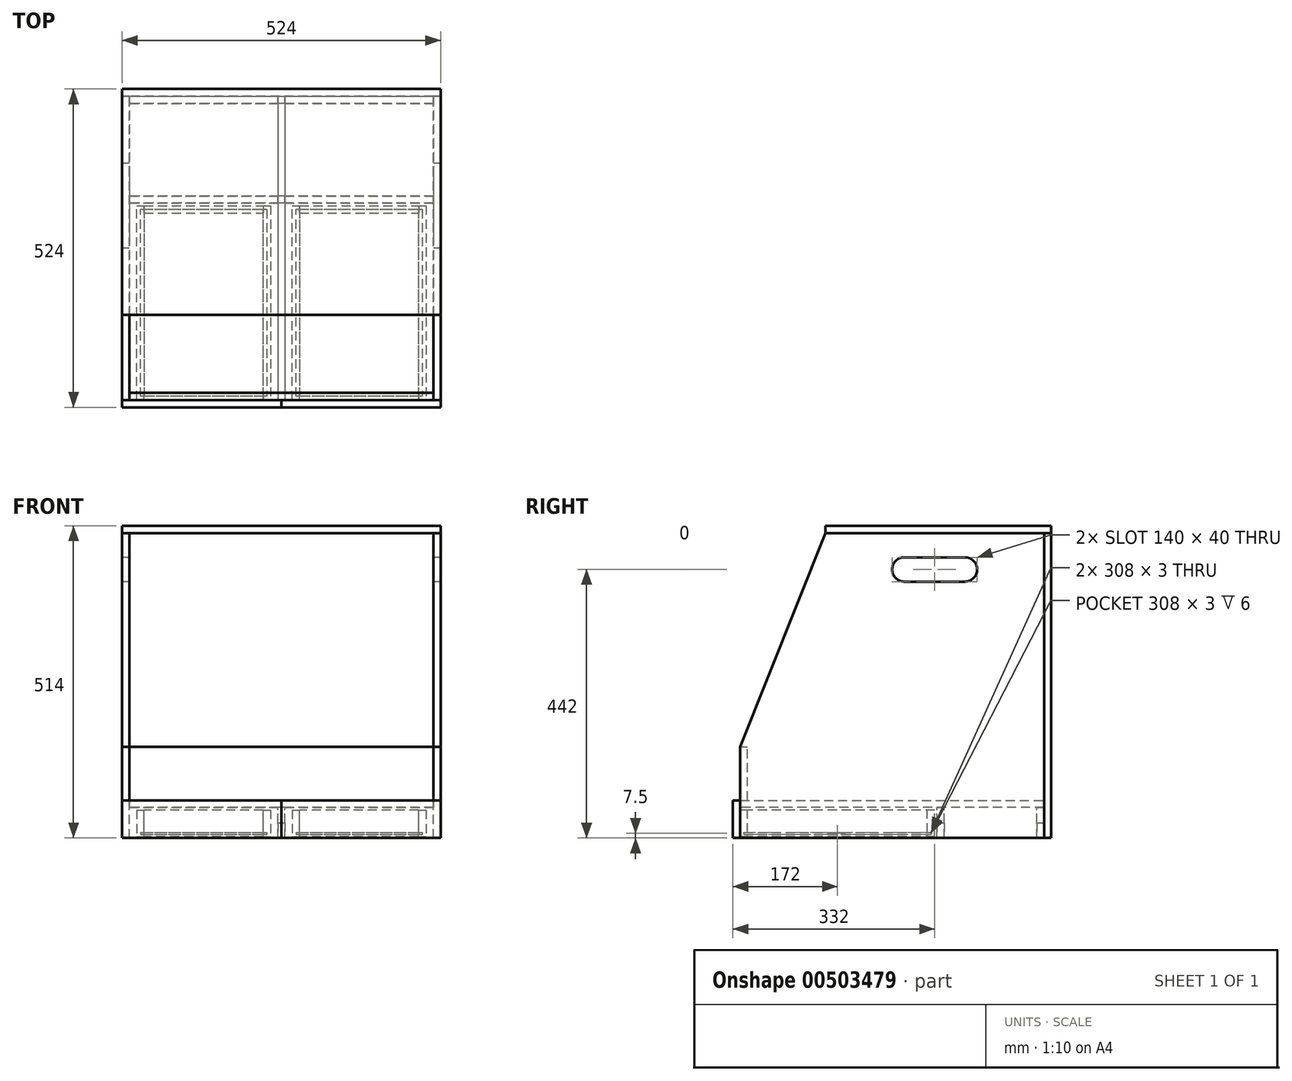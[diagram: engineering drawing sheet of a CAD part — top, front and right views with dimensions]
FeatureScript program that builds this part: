
annotation { "Feature Type Name" : "Feature", "Feature Type Description" : "" }
export const myFeature = defineFeature(function(context is Context, id is Id, definition is map)
    precondition{}
    {
        {
            var Q0;
            Q0=qCreatedBy(makeId("Top.planeOp"),FACE);
            var sketch = newSketch(context, id + "F0", { "sketchPlane" : qUnion([Q0])});
            skLineSegment(sketch, "E0.bottom", {"start": v(250, -250) * mm, "end": v(-250, -250) * mm});
            skLineSegment(sketch, "E0.top", {"start": v(250, 250) * mm, "end": v(-250, 250) * mm});
            skLineSegment(sketch, "E0.left", {"start": v(250, -250) * mm, "end": v(250, 250) * mm});
            skLineSegment(sketch, "E0.right", {"start": v(-250, -250) * mm, "end": v(-250, 250) * mm});
            skPoint(sketch, "E0.middle", {"position": v(0, 0) * mm});
            skSolve(sketch);
        }
        {
            var Q0;
            Q0 = qSketchRegion(id + "F0", true);
            extrude(context, id + "F1", {"entities" : qUnion([Q0]), "depth" : 12 * mm, "offsetDistance" : 25 * mm});
        }
        {
            var Q0;
            Q0=qCreatedBy(makeId("Right.planeOp"),FACE);
            var sketch = newSketch(context, id + "F2", { "sketchPlane" : qUnion([Q0])});
            skLineSegment(sketch, "E1.bottom", {"start": v(250, -25) * mm, "end": v(-250, -25) * mm});
            skLineSegment(sketch, "E1.top", {"start": v(250, 25) * mm, "end": v(-250, 25) * mm});
            skLineSegment(sketch, "E1.left", {"start": v(250, -25) * mm, "end": v(250, 25) * mm});
            skLineSegment(sketch, "E1.right", {"start": v(-250, -25) * mm, "end": v(-250, 25) * mm});
            skPoint(sketch, "E1.middle", {"position": v(0, 0) * mm});
            skSolve(sketch);
        }
        {
            var Q0;
            Q0 = qSketchRegion(id + "F2", true);
            extrude(context, id + "F3", {"entities" : qUnion([Q0]), "endBound" : BoundingType.SYMMETRIC, "depth" : 12 * mm, "offsetDistance" : 25 * mm});
        }
        {
            var Q0;
            Q0=makeQuery(id+"F3.opExtrude","SWEPT_BODY",BODY,{"disambiguationData":[OSD([sQuery(id+"F2.wireOp",EDGE,"E1.bottom"),sQuery(id+"F2.wireOp",EDGE,"E1.top"),sQuery(id+"F2.wireOp",EDGE,"E1.left"),sQuery(id+"F2.wireOp",EDGE,"E1.right")])]});
            transform(context, id + "F4", {"entities" : qUnion([Q0]), "transformType" : TransformType.TRANSLATION_3D, "dx" : 0 * mm, "dy" : 0 * mm, "dz" : -25 * mm, "makeCopy" : false});
        }
        {
            var Q0;
            Q0=qCreatedBy(makeId("Front.planeOp"),FACE);
            var sketch = newSketch(context, id + "F5", { "sketchPlane" : qUnion([Q0])});
            skLineSegment(sketch, "E2.bottom", {"start": v(250, -25) * mm, "end": v(-250, -25) * mm});
            skLineSegment(sketch, "E2.left", {"start": v(250, -25) * mm, "end": v(250, 25) * mm});
            skLineSegment(sketch, "E2.right", {"start": v(-250, -25) * mm, "end": v(-250, 25) * mm});
            skPoint(sketch, "E2.middle", {"position": v(0, 0) * mm});
            skLineSegment(sketch, "E3", {"start": v(-250, 25) * mm, "end": v(-6, 25) * mm});
            skLineSegment(sketch, "E4", {"start": v(-6, 25) * mm, "end": v(-6, 0) * mm});
            skLineSegment(sketch, "E5", {"start": v(-6, 0) * mm, "end": v(6, 0) * mm});
            skLineSegment(sketch, "E6", {"start": v(6, 0) * mm, "end": v(6, 25) * mm});
            skLineSegment(sketch, "E7", {"start": v(6, 25) * mm, "end": v(250, 25) * mm});
            skSolve(sketch);
        }
        {
            var Q0;
            Q0 = qSketchRegion(id + "F5", true);
            extrude(context, id + "F6", {"entities" : qUnion([Q0]), "endBound" : BoundingType.SYMMETRIC, "depth" : 12 * mm, "offsetDistance" : 25 * mm});
        }
        {
            var Q0;
            Q0=makeQuery(id+"F6.opExtrude","SWEPT_BODY",BODY,{"disambiguationData":[OSD([sQuery(id+"F5.wireOp",EDGE,"E2.bottom"),sQuery(id+"F5.wireOp",EDGE,"E2.top"),sQuery(id+"F5.wireOp",EDGE,"E2.left"),sQuery(id+"F5.wireOp",EDGE,"E2.right")])]});
            transform(context, id + "F7", {"entities" : qUnion([Q0]), "transformType" : TransformType.TRANSLATION_3D, "dx" : 0 * mm, "dy" : 80 * mm, "dz" : -25 * mm, "makeCopy" : false});
        }
        {
            var Q0;
            Q0=makeQuery(id+"F6.opExtrude","SWEPT_BODY",BODY,{"disambiguationData":[OSD([sQuery(id+"F5.wireOp",EDGE,"E2.bottom"),sQuery(id+"F5.wireOp",EDGE,"E2.top"),sQuery(id+"F5.wireOp",EDGE,"E2.left"),sQuery(id+"F5.wireOp",EDGE,"E2.right")])]});
            transform(context, id + "F8", {"entities" : qUnion([Q0]), "transformType" : TransformType.COPY});
        }
        {
            var Q0;
            Q0=makeQuery(id+"F8.opPattern","COPY",BODY,{"derivedFrom":makeQuery(id+"F6.opExtrude","SWEPT_BODY",BODY,{"disambiguationData":[OSD([sQuery(id+"F5.wireOp",EDGE,"E2.bottom"),sQuery(id+"F5.wireOp",EDGE,"E2.top"),sQuery(id+"F5.wireOp",EDGE,"E2.left"),sQuery(id+"F5.wireOp",EDGE,"E2.right")])]}),"instanceName":"1"});
            deleteBodies(context, id + "F9", {"entities" : qUnion([Q0])});
        }
        {
            var Q0;
            Q0=makeQuery(id+"F6.opExtrude","SWEPT_BODY",BODY,{"disambiguationData":[OSD([sQuery(id+"F5.wireOp",EDGE,"E2.bottom"),sQuery(id+"F5.wireOp",EDGE,"E2.left"),sQuery(id+"F5.wireOp",EDGE,"E2.right"),sQuery(id+"F5.wireOp",EDGE,"E3"),sQuery(id+"F5.wireOp",EDGE,"E4"),sQuery(id+"F5.wireOp",EDGE,"E5"),sQuery(id+"F5.wireOp",EDGE,"E6"),sQuery(id+"F5.wireOp",EDGE,"E7")])]});
            var Q1;
            Q1=makeQuery(id+"F3.opExtrude","SWEPT_BODY",BODY,{"disambiguationData":[OSD([sQuery(id+"F2.wireOp",EDGE,"E1.bottom"),sQuery(id+"F2.wireOp",EDGE,"E1.top"),sQuery(id+"F2.wireOp",EDGE,"E1.left"),sQuery(id+"F2.wireOp",EDGE,"E1.right")])]});
            booleanBodies(context, id + "F10", {"operationType" : BooleanOperationType.SUBTRACTION, "tools" : qUnion([Q0]), "targets" : qUnion([Q1]), "keepTools" : true});
        }
        {
            var Q0;
            Q0=makeQuery(id+"F6.opExtrude","SWEPT_BODY",BODY,{"disambiguationData":[OSD([sQuery(id+"F5.wireOp",EDGE,"E2.bottom"),sQuery(id+"F5.wireOp",EDGE,"E2.left"),sQuery(id+"F5.wireOp",EDGE,"E2.right"),sQuery(id+"F5.wireOp",EDGE,"E3"),sQuery(id+"F5.wireOp",EDGE,"E4"),sQuery(id+"F5.wireOp",EDGE,"E5"),sQuery(id+"F5.wireOp",EDGE,"E6"),sQuery(id+"F5.wireOp",EDGE,"E7")])]});
            transform(context, id + "F11", {"entities" : qUnion([Q0]), "transformType" : TransformType.TRANSLATION_3D, "dx" : 0 * mm, "dy" : 164 * mm, "dz" : 0 * mm, "makeCopy" : true});
        }
        {
            var Q0;
            Q0=makeQuery(id+"F11.opPattern","COPY",BODY,{"derivedFrom":makeQuery(id+"F6.opExtrude","SWEPT_BODY",BODY,{"disambiguationData":[OSD([sQuery(id+"F5.wireOp",EDGE,"E2.bottom"),sQuery(id+"F5.wireOp",EDGE,"E2.left"),sQuery(id+"F5.wireOp",EDGE,"E2.right"),sQuery(id+"F5.wireOp",EDGE,"E3"),sQuery(id+"F5.wireOp",EDGE,"E4"),sQuery(id+"F5.wireOp",EDGE,"E5"),sQuery(id+"F5.wireOp",EDGE,"E6"),sQuery(id+"F5.wireOp",EDGE,"E7")])]}),"instanceName":"1"});
            var Q1;
            Q1=makeQuery(id+"F3.opExtrude","SWEPT_BODY",BODY,{"disambiguationData":[OSD([sQuery(id+"F2.wireOp",EDGE,"E1.bottom"),sQuery(id+"F2.wireOp",EDGE,"E1.top"),sQuery(id+"F2.wireOp",EDGE,"E1.left"),sQuery(id+"F2.wireOp",EDGE,"E1.right")])]});
            booleanBodies(context, id + "F12", {"operationType" : BooleanOperationType.SUBTRACTION, "tools" : qUnion([Q0]), "targets" : qUnion([Q1]), "keepTools" : true});
        }
        {
            var Q0;
            Q0=qCreatedBy(makeId("Right.planeOp"),FACE);
            var sketch = newSketch(context, id + "F13", { "sketchPlane" : qUnion([Q0])});
            skLineSegment(sketch, "E8", {"start": v(0, 0) * mm, "end": v(250, 0) * mm});
            skLineSegment(sketch, "E9", {"start": v(250, 0) * mm, "end": v(250, -50) * mm});
            skLineSegment(sketch, "E10", {"start": v(250, -50) * mm, "end": v(-250, -50) * mm});
            skLineSegment(sketch, "E11", {"start": v(-250, -50) * mm, "end": v(-250, 100) * mm});
            skLineSegment(sketch, "E12", {"start": v(250, 0) * mm, "end": v(250, 452) * mm});
            skLineSegment(sketch, "E13", {"start": v(250, 452) * mm, "end": v(-110, 452) * mm});
            skLineSegment(sketch, "E14", {"start": v(-110, 452) * mm, "end": v(-250, 100) * mm});
            skLineSegment(sketch, "E15", {"start": v(250, 452) * mm, "end": v(70, 452) * mm});
            skLineSegment(sketch, "E16", {"start": v(70, 452) * mm, "end": v(70, 392) * mm});
            skLineSegment(sketch, "E17.bottom", {"start": v(140, 372) * mm, "end": v(0, 372) * mm});
            skLineSegment(sketch, "E17.top", {"start": v(140, 412) * mm, "end": v(0, 412) * mm});
            skLineSegment(sketch, "E17.left", {"start": v(140, 372) * mm, "end": v(140, 412) * mm});
            skLineSegment(sketch, "E17.right", {"start": v(0, 372) * mm, "end": v(0, 412) * mm});
            skPoint(sketch, "E17.middle", {"position": v(70, 392) * mm});
            skSolve(sketch);
        }
        {
            var Q0;
            Q0=makeQuery(id+"F13.imprint","IMPRINT",FACE,{"disambiguationData":[TD([[makeQuery(id+"F13.imprint","IMPRINT",EDGE,{"derivedFrom":sQuery(id+"F13.wireOp",EDGE,"E9")}),-1.0]])]});
            extrude(context, id + "F14", {"entities" : qUnion([Q0]), "endBound" : BoundingType.SYMMETRIC, "depth" : 12 * mm, "offsetDistance" : 25 * mm});
        }
        {
            var Q0;
            Q0=makeQuery(id+"F14.opExtrude","SWEPT_EDGE",EDGE,{"disambiguationData":[OSD([sQuery(id+"F13.wireOp",EDGE,"E17.bottom"),sQuery(id+"F13.wireOp",EDGE,"E17.left")])]});
            var Q1;
            Q1=makeQuery(id+"F14.opExtrude","SWEPT_EDGE",EDGE,{"disambiguationData":[OSD([sQuery(id+"F13.wireOp",EDGE,"E17.top"),sQuery(id+"F13.wireOp",EDGE,"E17.left")])]});
            var Q2;
            Q2=makeQuery(id+"F14.opExtrude","SWEPT_EDGE",EDGE,{"disambiguationData":[OSD([sQuery(id+"F13.wireOp",EDGE,"E17.top"),sQuery(id+"F13.wireOp",EDGE,"E17.right")])]});
            var Q3;
            Q3=makeQuery(id+"F14.opExtrude","SWEPT_EDGE",EDGE,{"disambiguationData":[OSD([sQuery(id+"F13.wireOp",EDGE,"E17.bottom"),sQuery(id+"F13.wireOp",EDGE,"E17.right")])]});
            fillet(context, id + "F15", {"entities" : qUnion([Q0, Q1, Q2, Q3]), "radius" : 20 * mm, "tangentPropagation" : true, "allowEdgeOverflow" : false});
        }
        {
            var Q0;
            Q0=makeQuery(id+"F14.opExtrude","SWEPT_BODY",BODY,{"disambiguationData":[OSD([sQuery(id+"F13.wireOp",EDGE,"E9"),sQuery(id+"F13.wireOp",EDGE,"E10"),sQuery(id+"F13.wireOp",EDGE,"E11"),sQuery(id+"F13.wireOp",EDGE,"E12"),sQuery(id+"F13.wireOp",EDGE,"E13"),sQuery(id+"F13.wireOp",EDGE,"E14"),sQuery(id+"F13.wireOp",EDGE,"E17.bottom"),sQuery(id+"F13.wireOp",EDGE,"E17.top"),sQuery(id+"F13.wireOp",EDGE,"E17.left"),sQuery(id+"F13.wireOp",EDGE,"E17.right")])]});
            transform(context, id + "F16", {"entities" : qUnion([Q0]), "transformType" : TransformType.TRANSLATION_3D, "dx" : -256 * mm, "dy" : 0 * mm, "dz" : 0 * mm, "makeCopy" : false});
        }
        {
            var Q0;
            Q0=makeQuery(id+"F14.opExtrude","SWEPT_BODY",BODY,{"disambiguationData":[OSD([sQuery(id+"F13.wireOp",EDGE,"E9"),sQuery(id+"F13.wireOp",EDGE,"E10"),sQuery(id+"F13.wireOp",EDGE,"E11"),sQuery(id+"F13.wireOp",EDGE,"E12"),sQuery(id+"F13.wireOp",EDGE,"E13"),sQuery(id+"F13.wireOp",EDGE,"E14"),sQuery(id+"F13.wireOp",EDGE,"E17.bottom"),sQuery(id+"F13.wireOp",EDGE,"E17.top"),sQuery(id+"F13.wireOp",EDGE,"E17.left"),sQuery(id+"F13.wireOp",EDGE,"E17.right")])]});
            transform(context, id + "F17", {"entities" : qUnion([Q0]), "transformType" : TransformType.TRANSLATION_3D, "dx" : 512 * mm, "dy" : 0 * mm, "dz" : 0 * mm, "makeCopy" : true});
        }
        {
            var Q0;
            Q0=qCreatedBy(makeId("Front.planeOp"),FACE);
            var sketch = newSketch(context, id + "F18", { "sketchPlane" : qUnion([Q0])});
            skLineSegment(sketch, "E18", {"start": v(0, 0) * mm, "end": v(-262, 0) * mm});
            skLineSegment(sketch, "E19", {"start": v(-262, 0) * mm, "end": v(-262, -50) * mm});
            skLineSegment(sketch, "E20", {"start": v(-262, -50) * mm, "end": v(262, -50) * mm});
            skLineSegment(sketch, "E21", {"start": v(262, -50) * mm, "end": v(262, 452) * mm});
            skLineSegment(sketch, "E22", {"start": v(262, 452) * mm, "end": v(-262, 452) * mm});
            skLineSegment(sketch, "E23", {"start": v(-262, 452) * mm, "end": v(-262, 0) * mm});
            skSolve(sketch);
        }
        {
            var Q0;
            Q0 = qSketchRegion(id + "F18", true);
            extrude(context, id + "F19", {"entities" : qUnion([Q0]), "endBound" : BoundingType.SYMMETRIC, "depth" : 12 * mm, "offsetDistance" : 25 * mm});
        }
        {
            var Q0;
            Q0=makeQuery(id+"F19.opExtrude","SWEPT_BODY",BODY,{"disambiguationData":[OSD([sQuery(id+"F18.wireOp",EDGE,"E19"),sQuery(id+"F18.wireOp",EDGE,"E20"),sQuery(id+"F18.wireOp",EDGE,"E21"),sQuery(id+"F18.wireOp",EDGE,"E22"),sQuery(id+"F18.wireOp",EDGE,"E23")])]});
            transform(context, id + "F20", {"entities" : qUnion([Q0]), "transformType" : TransformType.TRANSLATION_3D, "dx" : 0 * mm, "dy" : 256 * mm, "dz" : 0 * mm, "makeCopy" : false});
        }
        {
            var Q0;
            Q0=makeQuery(id+"F1.opExtrude","CAP_FACE",FACE,{"disambiguationData":[OSD([sQuery(id+"F0.wireOp",EDGE,"E0.bottom"),sQuery(id+"F0.wireOp",EDGE,"E0.top"),sQuery(id+"F0.wireOp",EDGE,"E0.left"),sQuery(id+"F0.wireOp",EDGE,"E0.right")])],"isStart":false});
            var sketch = newSketch(context, id + "F21", { "sketchPlane" : qUnion([Q0])});
            skLineSegment(sketch, "E24", {"start": v(0, 0) * mm, "end": v(0, 262) * mm});
            skLineSegment(sketch, "E25", {"start": v(0, 262) * mm, "end": v(262, 262) * mm});
            skLineSegment(sketch, "E26", {"start": v(262, 262) * mm, "end": v(262, -110) * mm});
            skLineSegment(sketch, "E27", {"start": v(262, -110) * mm, "end": v(-262, -110) * mm});
            skLineSegment(sketch, "E28", {"start": v(-262, -110) * mm, "end": v(-262, 262) * mm});
            skLineSegment(sketch, "E29", {"start": v(-262, 262) * mm, "end": v(0, 262) * mm});
            skSolve(sketch);
        }
        {
            var Q0;
            Q0 = qSketchRegion(id + "F21", true);
            extrude(context, id + "F22", {"entities" : qUnion([Q0]), "depth" : 12 * mm, "offsetDistance" : 25 * mm});
        }
        {
            var Q0;
            Q0=makeQuery(id+"F22.opExtrude","SWEPT_BODY",BODY,{"disambiguationData":[OSD([sQuery(id+"F21.wireOp",EDGE,"E25"),sQuery(id+"F21.wireOp",EDGE,"E26"),sQuery(id+"F21.wireOp",EDGE,"E27"),sQuery(id+"F21.wireOp",EDGE,"E28"),sQuery(id+"F21.wireOp",EDGE,"E29")])]});
            transform(context, id + "F23", {"entities" : qUnion([Q0]), "transformType" : TransformType.TRANSLATION_3D, "dx" : 0 * mm, "dy" : 0 * mm, "dz" : 440 * mm, "makeCopy" : false});
        }
        {
            var Q0;
            Q0=qCreatedBy(makeId("Front.planeOp"),FACE);
            var sketch = newSketch(context, id + "F24", { "sketchPlane" : qUnion([Q0])});
            skLineSegment(sketch, "E30", {"start": v(0, 0) * mm, "end": v(0, 12) * mm});
            skLineSegment(sketch, "E31", {"start": v(0, 12) * mm, "end": v(250, 12) * mm});
            skLineSegment(sketch, "E32", {"start": v(250, 12) * mm, "end": v(250, 100) * mm});
            skLineSegment(sketch, "E33", {"start": v(250, 100) * mm, "end": v(-250, 100) * mm});
            skLineSegment(sketch, "E34", {"start": v(-250, 100) * mm, "end": v(-250, 12) * mm});
            skLineSegment(sketch, "E35", {"start": v(-250, 12) * mm, "end": v(0, 12) * mm});
            skSolve(sketch);
        }
        {
            var Q0;
            Q0 = qSketchRegion(id + "F24", true);
            extrude(context, id + "F25", {"entities" : qUnion([Q0]), "endBound" : BoundingType.SYMMETRIC, "depth" : 12 * mm, "offsetDistance" : 25 * mm});
        }
        {
            var Q0;
            Q0=makeQuery(id+"F25.opExtrude","SWEPT_BODY",BODY,{"disambiguationData":[OSD([sQuery(id+"F24.wireOp",EDGE,"E31"),sQuery(id+"F24.wireOp",EDGE,"E32"),sQuery(id+"F24.wireOp",EDGE,"E33"),sQuery(id+"F24.wireOp",EDGE,"E34"),sQuery(id+"F24.wireOp",EDGE,"E35")])]});
            transform(context, id + "F26", {"entities" : qUnion([Q0]), "transformType" : TransformType.TRANSLATION_3D, "dx" : 0 * mm, "dy" : -244 * mm, "dz" : 0 * mm, "makeCopy" : false});
        }
        {
            var Q0;
            Q0=qCreatedBy(makeId("Top.planeOp"),FACE);
            var sketch = newSketch(context, id + "F27", { "sketchPlane" : qUnion([Q0])});
            skLineSegment(sketch, "E36", {"start": v(0, 0) * mm, "end": v(0, 70) * mm});
            skLineSegment(sketch, "E37", {"start": v(0, 70) * mm, "end": v(-18, 70) * mm});
            skLineSegment(sketch, "E38", {"start": v(-18, 70) * mm, "end": v(-18, -250) * mm});
            skLineSegment(sketch, "E39", {"start": v(-18, -250) * mm, "end": v(-30, -250) * mm});
            skLineSegment(sketch, "E40", {"start": v(-30, -250) * mm, "end": v(-30, 70) * mm});
            skLineSegment(sketch, "E41", {"start": v(-30, 70) * mm, "end": v(-18, 70) * mm});
            skSolve(sketch);
        }
        {
            var Q0;
            Q0 = qSketchRegion(id + "F27", true);
            extrude(context, id + "F28", {"entities" : qUnion([Q0]), "depth" : 44 * mm, "offsetDistance" : 25 * mm});
        }
        {
            var Q0;
            Q0=makeQuery(id+"F28.opExtrude","SWEPT_BODY",BODY,{"disambiguationData":[OSD([sQuery(id+"F27.wireOp",EDGE,"E38"),sQuery(id+"F27.wireOp",EDGE,"E39"),sQuery(id+"F27.wireOp",EDGE,"E40"),sQuery(id+"F27.wireOp",EDGE,"E41")])]});
            transform(context, id + "F29", {"entities" : qUnion([Q0]), "transformType" : TransformType.TRANSLATION_3D, "dx" : 0 * mm, "dy" : 0 * mm, "dz" : -48 * mm, "makeCopy" : false});
        }
        {
            var Q0;
            Q0=makeQuery(id+"F28.opExtrude","SWEPT_BODY",BODY,{"disambiguationData":[OSD([sQuery(id+"F27.wireOp",EDGE,"E38"),sQuery(id+"F27.wireOp",EDGE,"E39"),sQuery(id+"F27.wireOp",EDGE,"E40"),sQuery(id+"F27.wireOp",EDGE,"E41")])]});
            transform(context, id + "F30", {"entities" : qUnion([Q0]), "transformType" : TransformType.TRANSLATION_3D, "dx" : -208 * mm, "dy" : 0 * mm, "dz" : 0 * mm, "makeCopy" : true});
        }
        {
            var Q0;
            Q0=qCreatedBy(makeId("Top.planeOp"),FACE);
            var sketch = newSketch(context, id + "F31", { "sketchPlane" : qUnion([Q0])});
            skLineSegment(sketch, "E42", {"start": v(0, 0) * mm, "end": v(0, -250) * mm});
            skLineSegment(sketch, "E43", {"start": v(0, -250) * mm, "end": v(-30, -250) * mm});
            skLineSegment(sketch, "E44", {"start": v(-30, -250) * mm, "end": v(-226, -250) * mm});
            skLineSegment(sketch, "E45", {"start": v(-226, -250) * mm, "end": v(-226, -238) * mm});
            skLineSegment(sketch, "E46", {"start": v(-226, -238) * mm, "end": v(-30, -238) * mm});
            skLineSegment(sketch, "E47", {"start": v(-30, -238) * mm, "end": v(-30, -250) * mm});
            skSolve(sketch);
        }
        {
            var Q0;
            Q0 = qSketchRegion(id + "F31", true);
            extrude(context, id + "F32", {"entities" : qUnion([Q0]), "depth" : -44 * mm, "offsetDistance" : 25 * mm});
        }
        {
            var Q0;
            Q0=makeQuery(id+"F32.opExtrude","SWEPT_BODY",BODY,{"disambiguationData":[OSD([sQuery(id+"F31.wireOp",EDGE,"E44"),sQuery(id+"F31.wireOp",EDGE,"E45"),sQuery(id+"F31.wireOp",EDGE,"E46"),sQuery(id+"F31.wireOp",EDGE,"E47")])]});
            transform(context, id + "F33", {"entities" : qUnion([Q0]), "transformType" : TransformType.TRANSLATION_3D, "dx" : 0 * mm, "dy" : 0 * mm, "dz" : -4 * mm, "makeCopy" : false});
        }
        {
            var Q0;
            Q0=makeQuery(id+"F32.opExtrude","SWEPT_BODY",BODY,{"disambiguationData":[OSD([sQuery(id+"F31.wireOp",EDGE,"E44"),sQuery(id+"F31.wireOp",EDGE,"E45"),sQuery(id+"F31.wireOp",EDGE,"E46"),sQuery(id+"F31.wireOp",EDGE,"E47")])]});
            transform(context, id + "F34", {"entities" : qUnion([Q0]), "transformType" : TransformType.TRANSLATION_3D, "dx" : 0 * mm, "dy" : 308 * mm, "dz" : 0 * mm, "makeCopy" : true});
        }
        {
            var Q0;
            Q0=makeQuery(id+"F32.opExtrude","SWEPT_BODY",BODY,{"disambiguationData":[OSD([sQuery(id+"F31.wireOp",EDGE,"E44"),sQuery(id+"F31.wireOp",EDGE,"E45"),sQuery(id+"F31.wireOp",EDGE,"E46"),sQuery(id+"F31.wireOp",EDGE,"E47")])]});
            var Q1;
            Q1=makeQuery(id+"F30.opPattern","COPY",BODY,{"derivedFrom":makeQuery(id+"F28.opExtrude","SWEPT_BODY",BODY,{"disambiguationData":[OSD([sQuery(id+"F27.wireOp",EDGE,"E38"),sQuery(id+"F27.wireOp",EDGE,"E39"),sQuery(id+"F27.wireOp",EDGE,"E40"),sQuery(id+"F27.wireOp",EDGE,"E41")])]}),"instanceName":"1"});
            var Q2;
            Q2=makeQuery(id+"F28.opExtrude","SWEPT_BODY",BODY,{"disambiguationData":[OSD([sQuery(id+"F27.wireOp",EDGE,"E38"),sQuery(id+"F27.wireOp",EDGE,"E39"),sQuery(id+"F27.wireOp",EDGE,"E40"),sQuery(id+"F27.wireOp",EDGE,"E41")])]});
            var Q3;
            Q3=makeQuery(id+"F34.opPattern","COPY",BODY,{"derivedFrom":makeQuery(id+"F32.opExtrude","SWEPT_BODY",BODY,{"disambiguationData":[OSD([sQuery(id+"F31.wireOp",EDGE,"E44"),sQuery(id+"F31.wireOp",EDGE,"E45"),sQuery(id+"F31.wireOp",EDGE,"E46"),sQuery(id+"F31.wireOp",EDGE,"E47")])]}),"instanceName":"1"});
            transform(context, id + "F35", {"entities" : qUnion([Q0, Q1, Q2, Q3]), "transformType" : TransformType.TRANSLATION_3D, "dx" : 256 * mm, "dy" : 0 * mm, "dz" : 0 * mm, "makeCopy" : true});
        }
        {
            var Q0;
            Q0=qCreatedBy(makeId("Top.planeOp"),FACE);
            var sketch = newSketch(context, id + "F36", { "sketchPlane" : qUnion([Q0])});
            skLineSegment(sketch, "E48", {"start": v(0, 0) * mm, "end": v(-24, 0) * mm});
            skLineSegment(sketch, "E49", {"start": v(-24, 0) * mm, "end": v(-24, -244) * mm});
            skLineSegment(sketch, "E50", {"start": v(-24, -244) * mm, "end": v(-232, -244) * mm});
            skLineSegment(sketch, "E51", {"start": v(-232, -244) * mm, "end": v(-232, 64) * mm});
            skLineSegment(sketch, "E52", {"start": v(-232, 64) * mm, "end": v(-24, 64) * mm});
            skLineSegment(sketch, "E53", {"start": v(-24, 64) * mm, "end": v(-24, 0) * mm});
            skSolve(sketch);
        }
        {
            var Q0;
            Q0 = qSketchRegion(id + "F36", true);
            extrude(context, id + "F37", {"entities" : qUnion([Q0]), "depth" : 3 * mm, "offsetDistance" : 25 * mm});
        }
        {
            var Q0;
            Q0=makeQuery(id+"F37.opExtrude","SWEPT_BODY",BODY,{"disambiguationData":[OSD([sQuery(id+"F36.wireOp",EDGE,"E49"),sQuery(id+"F36.wireOp",EDGE,"E50"),sQuery(id+"F36.wireOp",EDGE,"E51"),sQuery(id+"F36.wireOp",EDGE,"E52"),sQuery(id+"F36.wireOp",EDGE,"E53")])]});
            transform(context, id + "F38", {"entities" : qUnion([Q0]), "transformType" : TransformType.TRANSLATION_3D, "dx" : 0 * mm, "dy" : 0 * mm, "dz" : -44 * mm, "makeCopy" : false});
        }
        {
            var Q0;
            Q0=makeQuery(id+"F37.opExtrude","SWEPT_BODY",BODY,{"disambiguationData":[OSD([sQuery(id+"F36.wireOp",EDGE,"E49"),sQuery(id+"F36.wireOp",EDGE,"E50"),sQuery(id+"F36.wireOp",EDGE,"E51"),sQuery(id+"F36.wireOp",EDGE,"E52"),sQuery(id+"F36.wireOp",EDGE,"E53")])]});
            transform(context, id + "F39", {"entities" : qUnion([Q0]), "transformType" : TransformType.TRANSLATION_3D, "dx" : 256 * mm, "dy" : 0 * mm, "dz" : 0 * mm, "makeCopy" : true});
        }
        {
            var Q0;
            Q0=makeQuery(id+"F37.opExtrude","SWEPT_BODY",BODY,{"disambiguationData":[OSD([sQuery(id+"F36.wireOp",EDGE,"E49"),sQuery(id+"F36.wireOp",EDGE,"E50"),sQuery(id+"F36.wireOp",EDGE,"E51"),sQuery(id+"F36.wireOp",EDGE,"E52"),sQuery(id+"F36.wireOp",EDGE,"E53")])]});
            var Q1;
            Q1=makeQuery(id+"F30.opPattern","COPY",BODY,{"derivedFrom":makeQuery(id+"F28.opExtrude","SWEPT_BODY",BODY,{"disambiguationData":[OSD([sQuery(id+"F27.wireOp",EDGE,"E38"),sQuery(id+"F27.wireOp",EDGE,"E39"),sQuery(id+"F27.wireOp",EDGE,"E40"),sQuery(id+"F27.wireOp",EDGE,"E41")])]}),"instanceName":"1"});
            var Q2;
            Q2=makeQuery(id+"F32.opExtrude","SWEPT_BODY",BODY,{"disambiguationData":[OSD([sQuery(id+"F31.wireOp",EDGE,"E44"),sQuery(id+"F31.wireOp",EDGE,"E45"),sQuery(id+"F31.wireOp",EDGE,"E46"),sQuery(id+"F31.wireOp",EDGE,"E47")])]});
            var Q3;
            Q3=makeQuery(id+"F28.opExtrude","SWEPT_BODY",BODY,{"disambiguationData":[OSD([sQuery(id+"F27.wireOp",EDGE,"E38"),sQuery(id+"F27.wireOp",EDGE,"E39"),sQuery(id+"F27.wireOp",EDGE,"E40"),sQuery(id+"F27.wireOp",EDGE,"E41")])]});
            var Q4;
            Q4=makeQuery(id+"F34.opPattern","COPY",BODY,{"derivedFrom":makeQuery(id+"F32.opExtrude","SWEPT_BODY",BODY,{"disambiguationData":[OSD([sQuery(id+"F31.wireOp",EDGE,"E44"),sQuery(id+"F31.wireOp",EDGE,"E45"),sQuery(id+"F31.wireOp",EDGE,"E46"),sQuery(id+"F31.wireOp",EDGE,"E47")])]}),"instanceName":"1"});
            booleanBodies(context, id + "F40", {"operationType" : BooleanOperationType.SUBTRACTION, "tools" : qUnion([Q0]), "targets" : qUnion([Q1, Q2, Q3, Q4]), "keepTools" : true});
        }
        {
            var Q0;
            Q0=makeQuery(id+"F39.opPattern","COPY",BODY,{"derivedFrom":makeQuery(id+"F37.opExtrude","SWEPT_BODY",BODY,{"disambiguationData":[OSD([sQuery(id+"F36.wireOp",EDGE,"E49"),sQuery(id+"F36.wireOp",EDGE,"E50"),sQuery(id+"F36.wireOp",EDGE,"E51"),sQuery(id+"F36.wireOp",EDGE,"E52"),sQuery(id+"F36.wireOp",EDGE,"E53")])]}),"instanceName":"1"});
            var Q1;
            Q1=makeQuery(id+"F35.opPattern","COPY",BODY,{"derivedFrom":makeQuery(id+"F32.opExtrude","SWEPT_BODY",BODY,{"disambiguationData":[OSD([sQuery(id+"F31.wireOp",EDGE,"E44"),sQuery(id+"F31.wireOp",EDGE,"E45"),sQuery(id+"F31.wireOp",EDGE,"E46"),sQuery(id+"F31.wireOp",EDGE,"E47")])]}),"instanceName":"1"});
            var Q2;
            Q2=makeQuery(id+"F35.opPattern","COPY",BODY,{"derivedFrom":makeQuery(id+"F28.opExtrude","SWEPT_BODY",BODY,{"disambiguationData":[OSD([sQuery(id+"F27.wireOp",EDGE,"E38"),sQuery(id+"F27.wireOp",EDGE,"E39"),sQuery(id+"F27.wireOp",EDGE,"E40"),sQuery(id+"F27.wireOp",EDGE,"E41")])]}),"instanceName":"1"});
            var Q3;
            Q3=makeQuery(id+"F35.opPattern","COPY",BODY,{"derivedFrom":makeQuery(id+"F34.opPattern","COPY",BODY,{"derivedFrom":makeQuery(id+"F32.opExtrude","SWEPT_BODY",BODY,{"disambiguationData":[OSD([sQuery(id+"F31.wireOp",EDGE,"E44"),sQuery(id+"F31.wireOp",EDGE,"E45"),sQuery(id+"F31.wireOp",EDGE,"E46"),sQuery(id+"F31.wireOp",EDGE,"E47")])]}),"instanceName":"1"}),"instanceName":"1"});
            var Q4;
            Q4=makeQuery(id+"F35.opPattern","COPY",BODY,{"derivedFrom":makeQuery(id+"F30.opPattern","COPY",BODY,{"derivedFrom":makeQuery(id+"F28.opExtrude","SWEPT_BODY",BODY,{"disambiguationData":[OSD([sQuery(id+"F27.wireOp",EDGE,"E38"),sQuery(id+"F27.wireOp",EDGE,"E39"),sQuery(id+"F27.wireOp",EDGE,"E40"),sQuery(id+"F27.wireOp",EDGE,"E41")])]}),"instanceName":"1"}),"instanceName":"1"});
            booleanBodies(context, id + "F41", {"operationType" : BooleanOperationType.SUBTRACTION, "tools" : qUnion([Q0]), "targets" : qUnion([Q1, Q2, Q3, Q4]), "keepTools" : true});
        }
        {
            var Q0;
            Q0=qCreatedBy(makeId("Front.planeOp"),FACE);
            var sketch = newSketch(context, id + "F42", { "sketchPlane" : qUnion([Q0])});
            skLineSegment(sketch, "E54", {"start": v(0, 0) * mm, "end": v(0, 12) * mm});
            skLineSegment(sketch, "E55", {"start": v(0, 12) * mm, "end": v(262, 12) * mm});
            skLineSegment(sketch, "E56", {"start": v(262, 12) * mm, "end": v(262, -50) * mm});
            skLineSegment(sketch, "E57", {"start": v(262, -50) * mm, "end": v(0, -50) * mm});
            skLineSegment(sketch, "E58", {"start": v(0, -50) * mm, "end": v(0, 0) * mm});
            skSolve(sketch);
        }
        {
            var Q0;
            Q0 = qSketchRegion(id + "F42", true);
            extrude(context, id + "F43", {"entities" : qUnion([Q0]), "depth" : 12 * mm, "offsetDistance" : 25 * mm});
        }
        {
            var Q0;
            Q0=makeQuery(id+"F43.opExtrude","SWEPT_BODY",BODY,{"disambiguationData":[OSD([sQuery(id+"F42.wireOp",EDGE,"E54"),sQuery(id+"F42.wireOp",EDGE,"E55"),sQuery(id+"F42.wireOp",EDGE,"E56"),sQuery(id+"F42.wireOp",EDGE,"E57"),sQuery(id+"F42.wireOp",EDGE,"E58")])]});
            transform(context, id + "F44", {"entities" : qUnion([Q0]), "transformType" : TransformType.TRANSLATION_3D, "dx" : 0 * mm, "dy" : -250 * mm, "dz" : 0 * mm, "makeCopy" : false});
        }
        {
            var Q0;
            Q0=makeQuery(id+"F43.opExtrude","SWEPT_BODY",BODY,{"disambiguationData":[OSD([sQuery(id+"F42.wireOp",EDGE,"E54"),sQuery(id+"F42.wireOp",EDGE,"E55"),sQuery(id+"F42.wireOp",EDGE,"E56"),sQuery(id+"F42.wireOp",EDGE,"E57"),sQuery(id+"F42.wireOp",EDGE,"E58")])]});
            transform(context, id + "F45", {"entities" : qUnion([Q0]), "transformType" : TransformType.TRANSLATION_3D, "dx" : -262 * mm, "dy" : 0 * mm, "dz" : 0 * mm, "makeCopy" : true});
        }
    });
